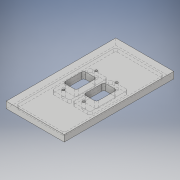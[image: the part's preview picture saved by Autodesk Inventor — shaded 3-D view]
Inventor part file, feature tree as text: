
AUTODESK INVENTOR PART (.ipt)
format: ipt  version: 2019.4 (Build 234330000, 330)  size: 210,432 bytes
history: native  units: in
note: dims shown in document units (in); Inventor stores cm internally (conversion verified against a paired STEP export)
features: sketch x4, extrude x3, hole x1
ambient origin geometry x8: Origin, YZ Plane, XZ Plane, XY Plane, X Axis, Y Axis, Z Axis, Center Point
bodies: Body1 (feature_tree)
feature tree (8):
  extrude  "Extrusion4"  Depth=4.5in
  hole  "Hole2"  [1 undecoded]
  extrude  "Extrusion5"  Depth=1.5748in
  extrude  "Extrusion6"  Depth=1.5748in
  sketch  "Sketch5"  dims[d44=8.5in d45=4.5in]
  sketch  "Sketch6"  dims[d46=0.5in d47=0.0in d48=1.2795in]
  sketch  "Sketch7"  dims[d49=0.7874in d51=2.5591in d52=0.7874in d54=1.5748in d57=0.7874in]
  sketch  "Sketch8"  dims[d58=0.1875in d59=0.2362in d60=0.4961in d61=0.0787in d62=90.0deg d63=0.315in d64=0.8108in d65=1.5748in d66=1.0in d67=0.1575in d68=0.7874in d70=1.5748in d71=0.3937in d73=0.3937in d75=0.0in d76=0.0in d77=0.3937in d78=0.3937in d79=0.1575in d80=2.9528in d81=0.7874in d82=1.378in d83=0.1575in d84=0.7874in d86=1.5748in d87=0.3937in d89=0.3937in d91=0.25in d92=0.0in]
note: 1 required parameter value undecoded (feature->parameter linkage not recoverable at this tier; creation-order binding heuristic only, values carry confidence <= 0.55)
